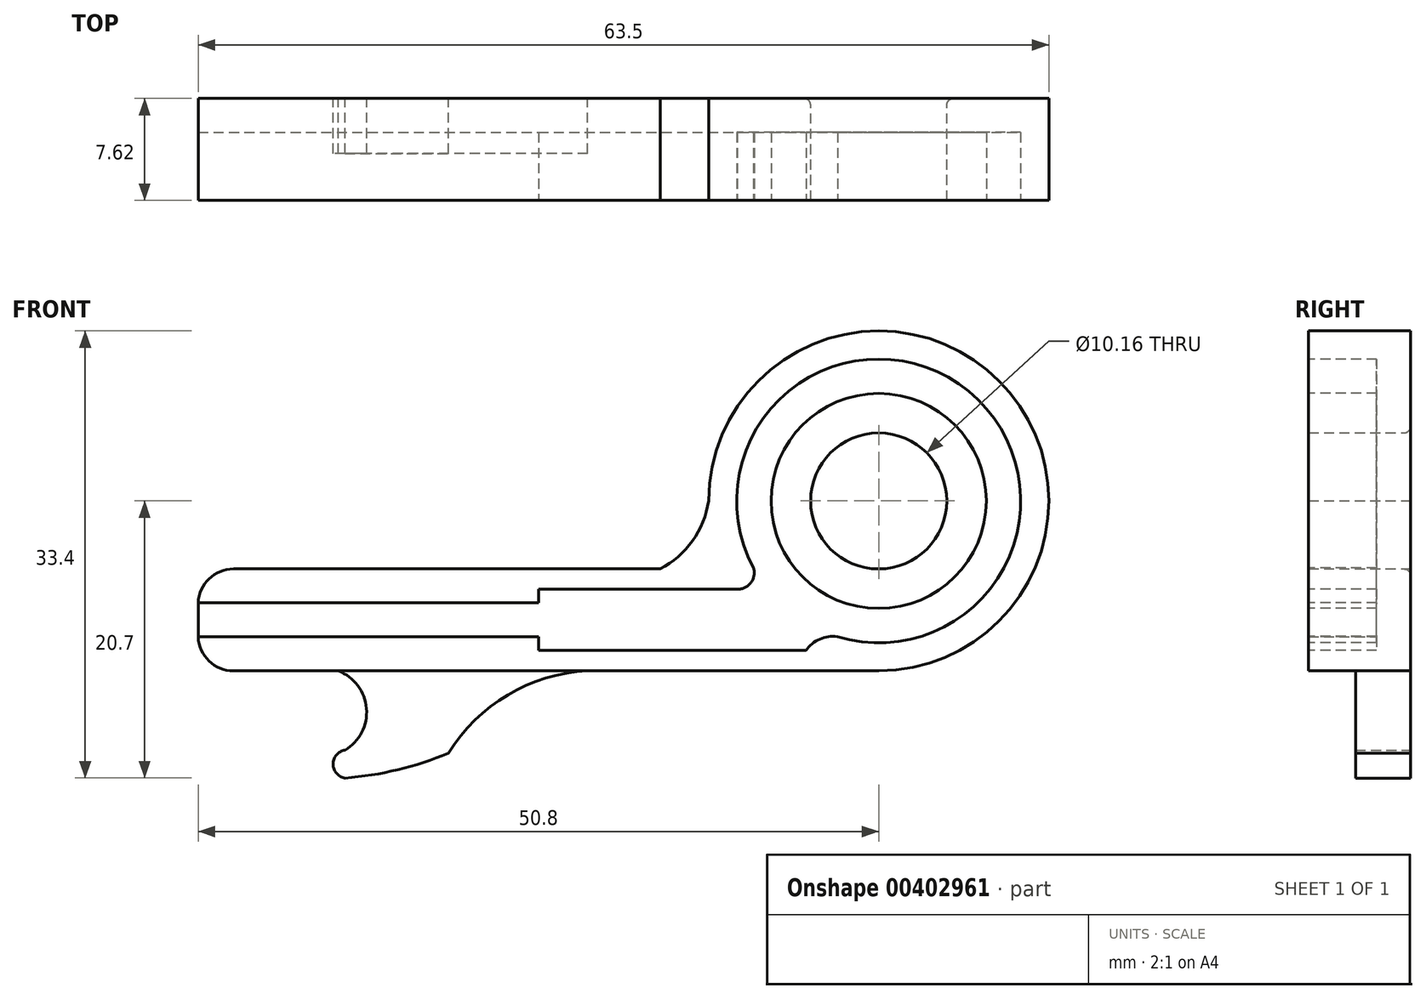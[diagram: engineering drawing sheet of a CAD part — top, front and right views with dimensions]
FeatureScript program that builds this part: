
annotation { "Feature Type Name" : "Feature", "Feature Type Description" : "" }
export const myFeature = defineFeature(function(context is Context, id is Id, definition is map)
    precondition{}
    {
        {
            var Q0;
            Q0=qCreatedBy(makeId("Front.planeOp"),FACE);
            var sketch = newSketch(context, id + "F0", { "sketchPlane" : qUnion([Q0])});
            skCircle(sketch, "E0", {"center": v(0, 0) * mm, "radius": 12.7 * mm});
            skCircle(sketch, "E1", {"center": v(0, 0) * mm, "radius": 5.08 * mm});
            skLineSegment(sketch, "E2", {"start": v(0, 0) * mm, "end": v(-76.2, 0) * mm, "construction": true});
            skLineSegment(sketch, "E3", {"start": v(0, -12.7) * mm, "end": v(-50.8, -12.7) * mm});
            skLineSegment(sketch, "E4", {"start": v(-50.8, -12.7) * mm, "end": v(-50.8, -5.08) * mm});
            skLineSegment(sketch, "E5", {"start": v(-50.8, -5.08) * mm, "end": v(-16.32, -5.08) * mm});
            skArc(sketch, "E6", {"start": v(-16.32, -5.08) * mm, "mid": v(-13.9, -2.98) * mm, "end": v(-12.7, 0) * mm});
            skSolve(sketch);
        }
        {
            var Q0;
            Q0=makeQuery(id+"F0.imprint","IMPRINT",FACE,{"disambiguationData":[TD([[makeQuery(id+"F0.imprint","IMPRINT",EDGE,{"derivedFrom":sQuery(id+"F0.wireOp",EDGE,"E1")}),-1.0]])]});
            var Q1;
            {var subQ0=sQuery(id+"F0.wireOp",EDGE,"E3");Q1=makeQuery(id+"F0.imprint","IMPRINT",FACE,{"disambiguationData":[TD([[makeQuery(id+"F0.imprint","IMPRINT",EDGE,{"derivedFrom":subQ0}),-1.0]])]});}
            extrude(context, id + "F1", {"entities" : qUnion([Q0, Q1]), "depth" : 7.62 * mm});
        }
        {
            var Q0;
            Q0=makeQuery(id+"F1.opExtrude","CAP_FACE",FACE,{"disambiguationData":[OSD([sQuery(id+"F0.wireOp",EDGE,"E0"),sQuery(id+"F0.wireOp",EDGE,"E1"),sQuery(id+"F0.wireOp",EDGE,"E3"),sQuery(id+"F0.wireOp",EDGE,"E4"),sQuery(id+"F0.wireOp",EDGE,"E5"),sQuery(id+"F0.wireOp",EDGE,"E6")])],"isStart":false});
            var sketch = newSketch(context, id + "F2", { "sketchPlane" : qUnion([Q0])});
            skLineSegment(sketch, "E7.bottom", {"start": v(-50.8, -7.62) * mm, "end": v(-25.4, -7.62) * mm});
            skLineSegment(sketch, "E7.top", {"start": v(-50.8, -10.16) * mm, "end": v(-25.4, -10.16) * mm});
            skLineSegment(sketch, "E7.left", {"start": v(-50.8, -7.62) * mm, "end": v(-50.8, -10.16) * mm});
            skPoint(sketch, "E8", {"position": v(-50.8, -8.9) * mm});
            skPoint(sketch, "E9", {"position": v(-25.4, -8.9) * mm});
            skLineSegment(sketch, "E10.bottom", {"start": v(-25.4, -6.6) * mm, "end": v(-10.52, -6.6) * mm});
            skLineSegment(sketch, "E10.top", {"start": v(-25.4, -11.18) * mm, "end": v(-5.42, -11.18) * mm});
            skCircle(sketch, "E11", {"center": v(0, 0) * mm, "radius": 8.03 * mm});
            skArc(sketch, "E12", {"start": v(-3.08, -10.14) * mm, "mid": v(6.73, 8.2) * mm, "end": v(-9.35, -5) * mm});
            skLineSegment(sketch, "E13.trimOffspring", {"start": v(-25.4, -10.16) * mm, "end": v(-25.4, -11.18) * mm});
            skArc(sketch, "E14", {"start": v(-3.08, -10.14) * mm, "mid": v(-4.4, -10.32) * mm, "end": v(-5.42, -11.18) * mm});
            skPoint(sketch, "E14.startSnap0", {"position": v(-5.42, -10.14) * mm});
            skArc(sketch, "E15", {"start": v(-10.55, -6.6) * mm, "mid": v(-9.54, -6.1) * mm, "end": v(-9.35, -5) * mm});
            skPoint(sketch, "E16.orphan", {"position": v(-5.42, -9.1) * mm});
            skLineSegment(sketch, "E17", {"start": v(-25.4, -6.6) * mm, "end": v(-25.4, -7.62) * mm});
            skSolve(sketch);
        }
        {
            var Q0;
            Q0=makeQuery(id+"F2.imprint","IMPRINT",FACE,{"disambiguationData":[TD([[makeQuery(id+"F2.imprint","IMPRINT",EDGE,{"derivedFrom":sQuery(id+"F2.wireOp",EDGE,"E7.bottom")}),-1.0]])]});
            extrude(context, id + "F3", {"entities" : qUnion([Q0]), "operationType" : NewBodyOperationType.REMOVE, "oppositeDirection" : true, "depth" : 5.08 * mm});
        }
        {
            var Q0;
            Q0=makeQuery(id+"F1.opExtrude","SWEPT_EDGE",EDGE,{"disambiguationData":[OSD([sQuery(id+"F0.wireOp",EDGE,"E4"),sQuery(id+"F0.wireOp",EDGE,"E5")])]});
            var Q1;
            Q1=makeQuery(id+"F1.opExtrude","SWEPT_EDGE",EDGE,{"disambiguationData":[OSD([sQuery(id+"F0.wireOp",EDGE,"E3"),sQuery(id+"F0.wireOp",EDGE,"E4")])]});
            fillet(context, id + "F4", {"entities" : qUnion([Q0, Q1]), "radius" : 2.64 * mm, "tangentPropagation" : true, "allowEdgeOverflow" : false});
        }
        {
            var Q0;
            Q0=makeQuery(id+"F1.opExtrude","CAP_EDGE",EDGE,{"disambiguationData":[OSD([sQuery(id+"F0.wireOp",EDGE,"E1")])],"isStart":true});
            fillet(context, id + "F5", {"entities" : qUnion([Q0]), "radius" : 0.5 * mm, "tangentPropagation" : true, "allowEdgeOverflow" : false});
        }
        {
            var Q0;
            Q0=qCreatedBy(makeId("Front.planeOp"),FACE);
            var sketch = newSketch(context, id + "F6", { "sketchPlane" : qUnion([Q0])});
            skArc(sketch, "E18", {"start": v(-39.84, -18.62) * mm, "mid": v(-38.24, -15.45) * mm, "end": v(-40.44, -12.66) * mm});
            skArc(sketch, "E19", {"start": v(-39.84, -18.62) * mm, "mid": v(-40.72, -19.66) * mm, "end": v(-39.84, -20.7) * mm});
            skArc(sketch, "E20", {"start": v(-39.84, -20.7) * mm, "mid": v(-35.9, -20.08) * mm, "end": v(-32.12, -18.84) * mm});
            skArc(sketch, "E21", {"start": v(-21.08, -12.68) * mm, "mid": v(-27.4, -14.33) * mm, "end": v(-32.12, -18.84) * mm});
            skLineSegment(sketch, "E22", {"start": v(-40.44, -12.66) * mm, "end": v(-21.08, -12.68) * mm});
            skSolve(sketch);
        }
        {
            var Q0;
            Q0=makeQuery(id+"F6.imprint","IMPRINT",FACE,{"disambiguationData":[TD([[makeQuery(id+"F6.imprint","IMPRINT",EDGE,{"derivedFrom":sQuery(id+"F6.wireOp",EDGE,"E18")}),-1.0]])]});
            extrude(context, id + "F7", {"entities" : qUnion([Q0]), "operationType" : NewBodyOperationType.ADD, "depth" : 4.11 * mm});
        }
    });
